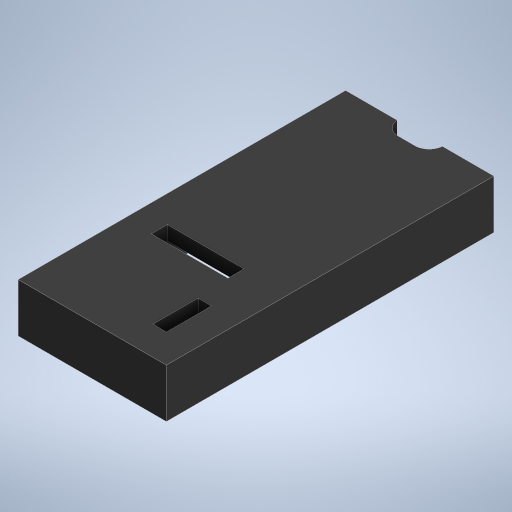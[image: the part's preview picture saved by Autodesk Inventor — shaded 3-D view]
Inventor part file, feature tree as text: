
AUTODESK INVENTOR PART (.ipt)
format: ipt  version: 2024 (Build 280153000, 153)  size: 275,456 bytes
history: native  units: in
note: dims shown in document units (in); Inventor stores cm internally (conversion verified against a paired STEP export)
features: extrude x3, sketch x3, projected_geometry x2, fillet x1
ambient origin geometry x8: Origin, YZ Plane, XZ Plane, XY Plane, X Axis, Y Axis, Z Axis, Center Point
bodies: Solid1 (feature_tree)
feature tree (9):
  extrude  "Extrusion1"  Depth=2.6in
  extrude  "Extrusion2"  Depth=0.125in
  extrude  "Extrusion3"  Depth=0.3in TaperAngle=0.0deg
  fillet  "Fillet2"  Radius=0.125in
  sketch  "Sketch1"  dims[d0=1.04in d1=2.6in]
  sketch  "Sketch2"  dims[d2=0.125in d3=0.1969in]
  sketch  "Sketch3"  dims[d4=0.1969in d5=0.3in d6=0.0in d8=0.125in d9=0.1181in d10=0.3937in d11=0.0197in d12=0.28in d13=0.125in d14=0.0in d15=0.125in d16=0.0in d18=0.115in d19=0.125in]
  projected_geometry  "Projected Loop1"
  projected_geometry  "Projected Loop2"
